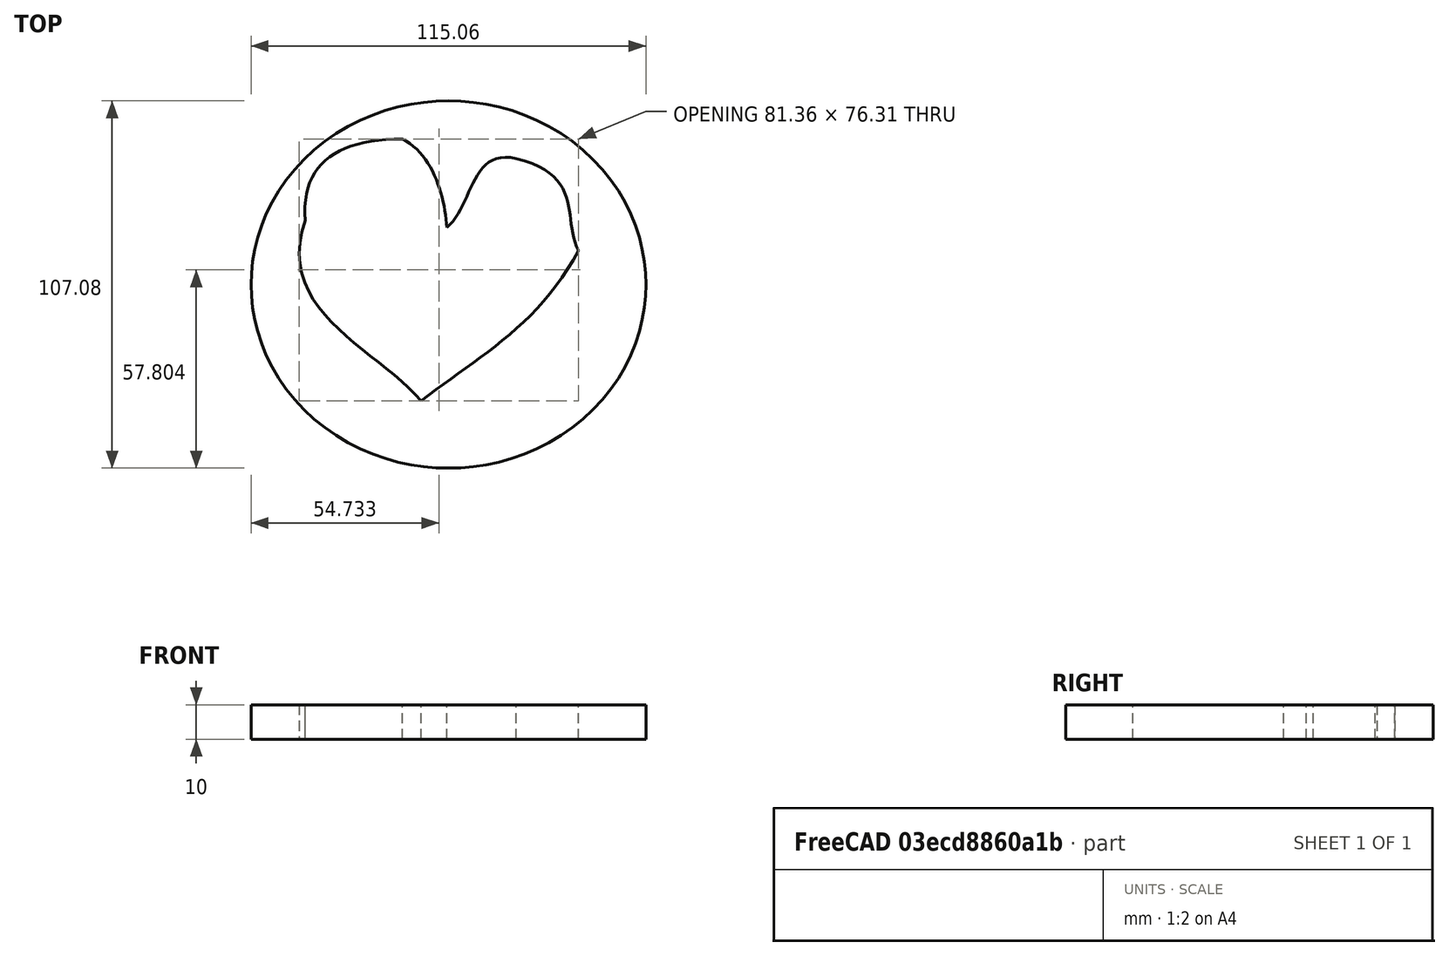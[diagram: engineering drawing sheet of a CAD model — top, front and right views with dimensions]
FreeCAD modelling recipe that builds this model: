
FCSTD DOCUMENT  (FreeCAD 0.20R29410 (Git))
Label: croqueada1
License: All rights reserved
LicenseURL: http://en.wikipedia.org/wiki/All_rights_reserved
objects: Part::Feature×2, Part::Extrusion×2, Part::Cut×1
note: 5 computed .brp shape members not serialized (recipe doc carries the construction recipe); baked Part::Feature solids carry a one-line shape summary decoded from their .brp

FEATURE [Part::Feature] path1865
  shape: bbox 87.21 x 76.4 x 2e-07 mm, 0 faces, 0 solids (baked)
FEATURE [Part::Feature] path1865001
  shape: bbox 115.1 x 107.1 x 2e-07 mm, 0 faces, 0 solids (baked)
FEATURE [Part::Extrusion] Extrude
  Base = -> path1865
  Dir = (0,0,1)
  DirMode = 2
  FaceMakerClass = Part::FaceMakerBullseye
  LengthFwd = 10
  LengthRev = 0
  Placement = pos=(0,0,-10) rot=(0,0,1;0rad)
  Solid = true
  Symmetric = false
FEATURE [Part::Extrusion] Extrude001
  Base = -> path1865001
  Dir = (0,0,-1)
  DirMode = 2
  FaceMakerClass = Part::FaceMakerBullseye
  LengthFwd = 10
  LengthRev = 0
  Solid = true
  Symmetric = false
FEATURE [Part::Cut] Cut
  Base = -> Extrude001
  Refine = true
  Tool = -> Extrude
